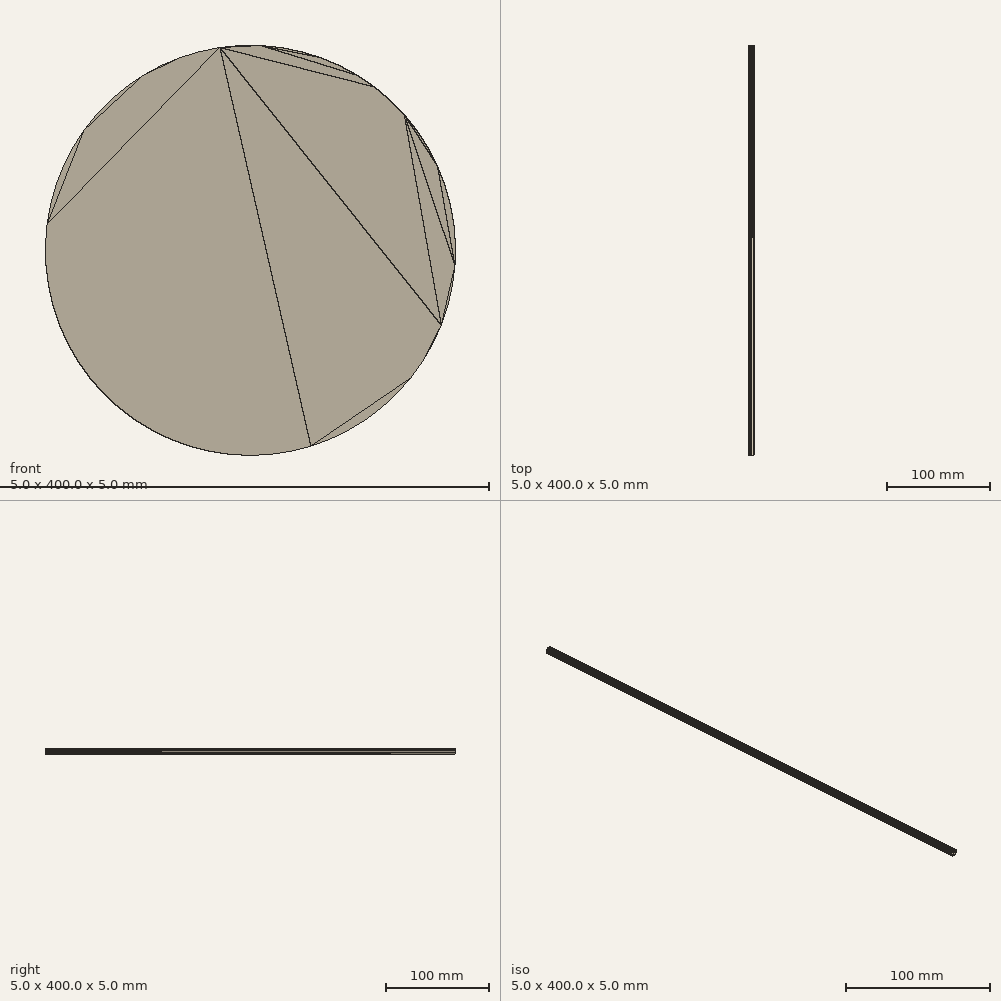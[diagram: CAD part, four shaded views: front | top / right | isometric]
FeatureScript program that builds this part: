
annotation { "Feature Type Name" : "Feature", "Feature Type Description" : "" }
export const myFeature = defineFeature(function(context is Context, id is Id, definition is map)
    precondition{}
    {
        {
            var Q0;
            Q0=qCreatedBy(makeId("Front.planeOp"),FACE);
            var sketch = newSketch(context, id + "F0", { "sketchPlane" : qUnion([Q0])});
            skCircle(sketch, "E0", {"center": v(0, 0) * mm, "radius": 2.5 * mm});
            skSolve(sketch);
        }
        {
            var Q0;
            Q0=qSketchRegion(id+"F0",true);
            extrude(context, id + "F1", {"entities" : qUnion([Q0]), "endBound" : BoundingType.SYMMETRIC, "depth" : 400 * mm, "offsetDistance" : 25 * mm});
        }
    });
